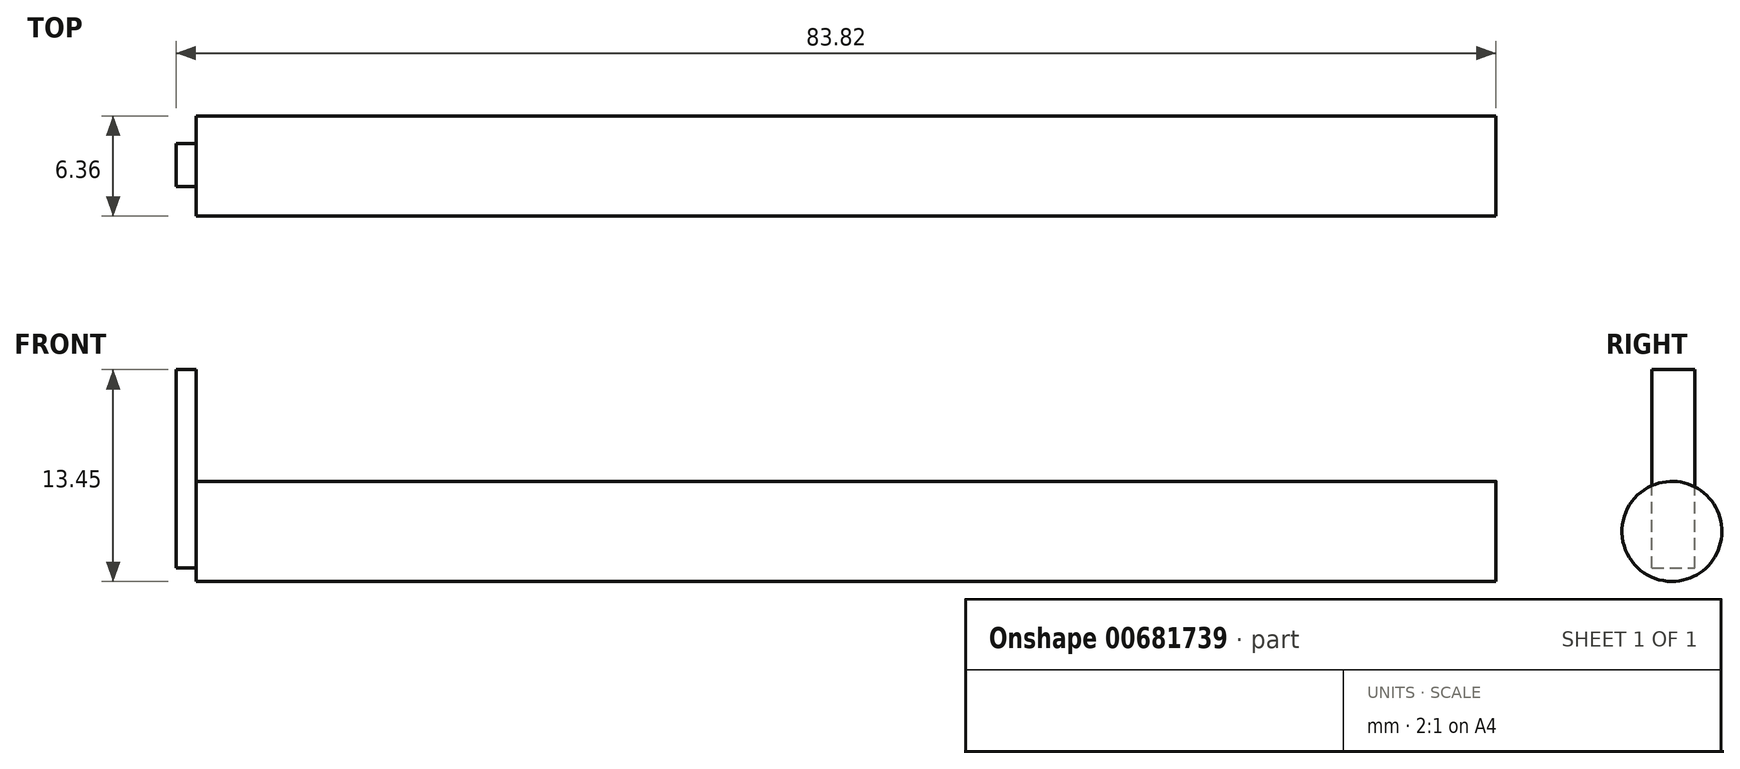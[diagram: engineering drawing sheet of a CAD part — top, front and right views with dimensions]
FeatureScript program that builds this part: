
annotation { "Feature Type Name" : "Feature", "Feature Type Description" : "" }
export const myFeature = defineFeature(function(context is Context, id is Id, definition is map)
    precondition{}
    {
        {
            var Q0;
            Q0=qCreatedBy(makeId("Right.planeOp"),FACE);
            var sketch = newSketch(context, id + "F0", { "sketchPlane" : qUnion([Q0])});
            skCircle(sketch, "E0", {"center": v(0, 0) * mm, "radius": 3.17 * mm});
            skSolve(sketch);
        }
        {
            var Q0;
            Q0 = qSketchRegion(id + "F0", true);
            extrude(context, id + "F1", {"entities" : qUnion([Q0]), "depth" : 82.55 * mm, "offsetDistance" : 25.4 * mm});
        }
        {
            var Q0;
            Q0=makeQuery(id+"F0.imprint","IMPRINT",FACE,{"disambiguationData":[TD([[makeQuery(id+"F0.imprint","IMPRINT",EDGE,{"derivedFrom":sQuery(id+"F0.wireOp",EDGE,"E0")}),1.0]])]});
            var sketch = newSketch(context, id + "F2", { "sketchPlane" : qUnion([Q0])});
            skLineSegment(sketch, "E1.bottom", {"start": v(-1.28, 1.48) * mm, "end": v(1.45, 1.48) * mm});
            skLineSegment(sketch, "E1.top", {"start": v(-1.28, 2.65) * mm, "end": v(1.45, 2.65) * mm});
            skLineSegment(sketch, "E1.left", {"start": v(-1.28, 1.48) * mm, "end": v(-1.28, 2.65) * mm});
            skLineSegment(sketch, "E1.right", {"start": v(1.45, 1.48) * mm, "end": v(1.45, 2.65) * mm});
            skSolve(sketch);
        }
        {
            var Q0;
            Q0 = qSketchRegion(id + "F2", true);
            extrude(context, id + "F3", {"entities" : qUnion([Q0]), "operationType" : NewBodyOperationType.ADD, "oppositeDirection" : true, "depth" : 1.27 * mm, "offsetDistance" : 25.4 * mm});
        }
        {
            var Q0;
            Q0=makeQuery(id+"F3.opExtrude","SWEPT_FACE",FACE,{"disambiguationData":[OSD([sQuery(id+"F2.wireOp",EDGE,"E1.top")])]});
            var sketch = newSketch(context, id + "F4", { "sketchPlane" : qUnion([Q0])});
            skLineSegment(sketch, "E2.bottom", {"start": v(-1.27, 1.45) * mm, "end": v(0, 1.45) * mm});
            skLineSegment(sketch, "E2.top", {"start": v(-1.27, -1.28) * mm, "end": v(0, -1.28) * mm});
            skLineSegment(sketch, "E2.left", {"start": v(-1.27, 1.45) * mm, "end": v(-1.27, -1.28) * mm});
            skLineSegment(sketch, "E2.right", {"start": v(0, 1.45) * mm, "end": v(0, -1.28) * mm});
            skSolve(sketch);
        }
        {
            var Q0;
            Q0 = qSketchRegion(id + "F4", true);
            extrude(context, id + "F5", {"entities" : qUnion([Q0]), "operationType" : NewBodyOperationType.ADD, "depth" : 7.62 * mm, "offsetDistance" : 25.4 * mm});
        }
        {
            var Q0;
            Q0=makeQuery(id+"F3.opExtrude","SWEPT_FACE",FACE,{"disambiguationData":[OSD([sQuery(id+"F2.wireOp",EDGE,"E1.bottom")])]});
            var sketch = newSketch(context, id + "F6", { "sketchPlane" : qUnion([Q0])});
            skLineSegment(sketch, "E3.bottom", {"start": v(-1.27, -1.45) * mm, "end": v(0, -1.45) * mm});
            skLineSegment(sketch, "E3.top", {"start": v(-1.27, 1.28) * mm, "end": v(0, 1.28) * mm});
            skLineSegment(sketch, "E3.left", {"start": v(-1.27, -1.45) * mm, "end": v(-1.27, 1.28) * mm});
            skLineSegment(sketch, "E3.right", {"start": v(0, -1.45) * mm, "end": v(0, 1.28) * mm});
            skSolve(sketch);
        }
        {
            var Q0;
            Q0 = qSketchRegion(id + "F6", true);
            extrude(context, id + "F7", {"entities" : qUnion([Q0]), "operationType" : NewBodyOperationType.ADD, "depth" : 3.8 * mm, "offsetDistance" : 25.4 * mm});
        }
    });
